# Revit family: DF_ДержательПроводникаКруглого_16_EZETEK
name_source: partatom
category: Соединительные детали воздуховодов
revit_build: Autodesk Revit 2017 (Build: 20170118_1100(x64)
units: mm (PartAtom-declared; Revit-internal decimal feet)

## family parameters
Всегда вертикально = Да
На основе рабочей плоскости = Нет
Общий = Нет
При загрузке вырезать с полостями = Нет
Размер круглого соединителя = Использовать радиус
Тип детали = Соединение

## types (12) — shared parameters
ADSK_Версия Revit = 2017
ADSK_Единица измерения = Неспецифицируемое
ADSK_Завод-изготовитель = Неспецифицируемое
ADSK_Код изделия = Неспецифицируемое
ADSK_Марка = Неспецифицируемое
ADSK_Масса_Текст = Неспецифицируемое
ADSK_Материал = BIMLIB_Латунь_EZETEK
ADSK_Наименование = Неспецифицируемое
ADSK_Обозначение = Неспецифицируемое
URL = https://ezetek.ru
Группа модели = Держатели
Изготовитель = Ezetek
Описание = Держатель закрепляет пруток молниезащитной сетки диаметром 6-8 мм на кровле и/или фасаде здания. Расстояние от прутка до основания держателя составляет 16 мм.
Угол = 90.00°
zero-valued in all types: ADSK_Количество, ADSK_Масса

## per-type parameters (varying)
| type | Тип |
| ДержательПроводникаКруглого_16_6-8_70088 | FA_ДержательПроводникаКруглого_16_EZETEK : ДержательПроводникаКруглого_16_6-8_70088 |
| ДержательПроводникаКруглого_16_6-8_70078 | FA_ДержательПроводникаКруглого_16_EZETEK : ДержательПроводникаКруглого_16_6-8_70078 |
| ДержательПроводникаКруглого_16_6-8_70068 | FA_ДержательПроводникаКруглого_16_EZETEK : ДержательПроводникаКруглого_16_6-8_70068 |
| ДержательПроводникаКруглого_16_6-8_70058 | FA_ДержательПроводникаКруглого_16_EZETEK : ДержательПроводникаКруглого_16_6-8_70058 |
| ДержательПроводникаКруглого_16_6-8_70048 | FA_ДержательПроводникаКруглого_16_EZETEK : ДержательПроводникаКруглого_16_6-8_70048 |
| ДержательПроводникаКруглого_16_6-8_70038 | FA_ДержательПроводникаКруглого_16_EZETEK : ДержательПроводникаКруглого_16_6-8_70038 |
| ДержательПроводникаКруглого_16_6-8_70028 | FA_ДержательПроводникаКруглого_16_EZETEK : ДержательПроводникаКруглого_16_6-8_70028 |
| ДержательПроводникаКруглого_16_6-8_70018 | FA_ДержательПроводникаКруглого_16_EZETEK : ДержательПроводникаКруглого_16_6-8_70018 |
| ДержательПроводникаКруглого_16_6-8_91005 | FA_ДержательПроводникаКруглого_16_EZETEK : ДержательПроводникаКруглого_16_6-8_91005 |
| ДержательПроводникаКруглого_16_6-8_91007 | FA_ДержательПроводникаКруглого_16_EZETEK : ДержательПроводникаКруглого_16_6-8_91007 |
| ДержательПроводникаКруглого_16_6-8_91002 | FA_ДержательПроводникаКруглого_16_EZETEK : ДержательПроводникаКруглого_16_6-8_91002 |
| ДержательПроводникаКруглого_16_6-8_91001 | FA_ДержательПроводникаКруглого_16_EZETEK : ДержательПроводникаКруглого_16_6-8_91001 |
